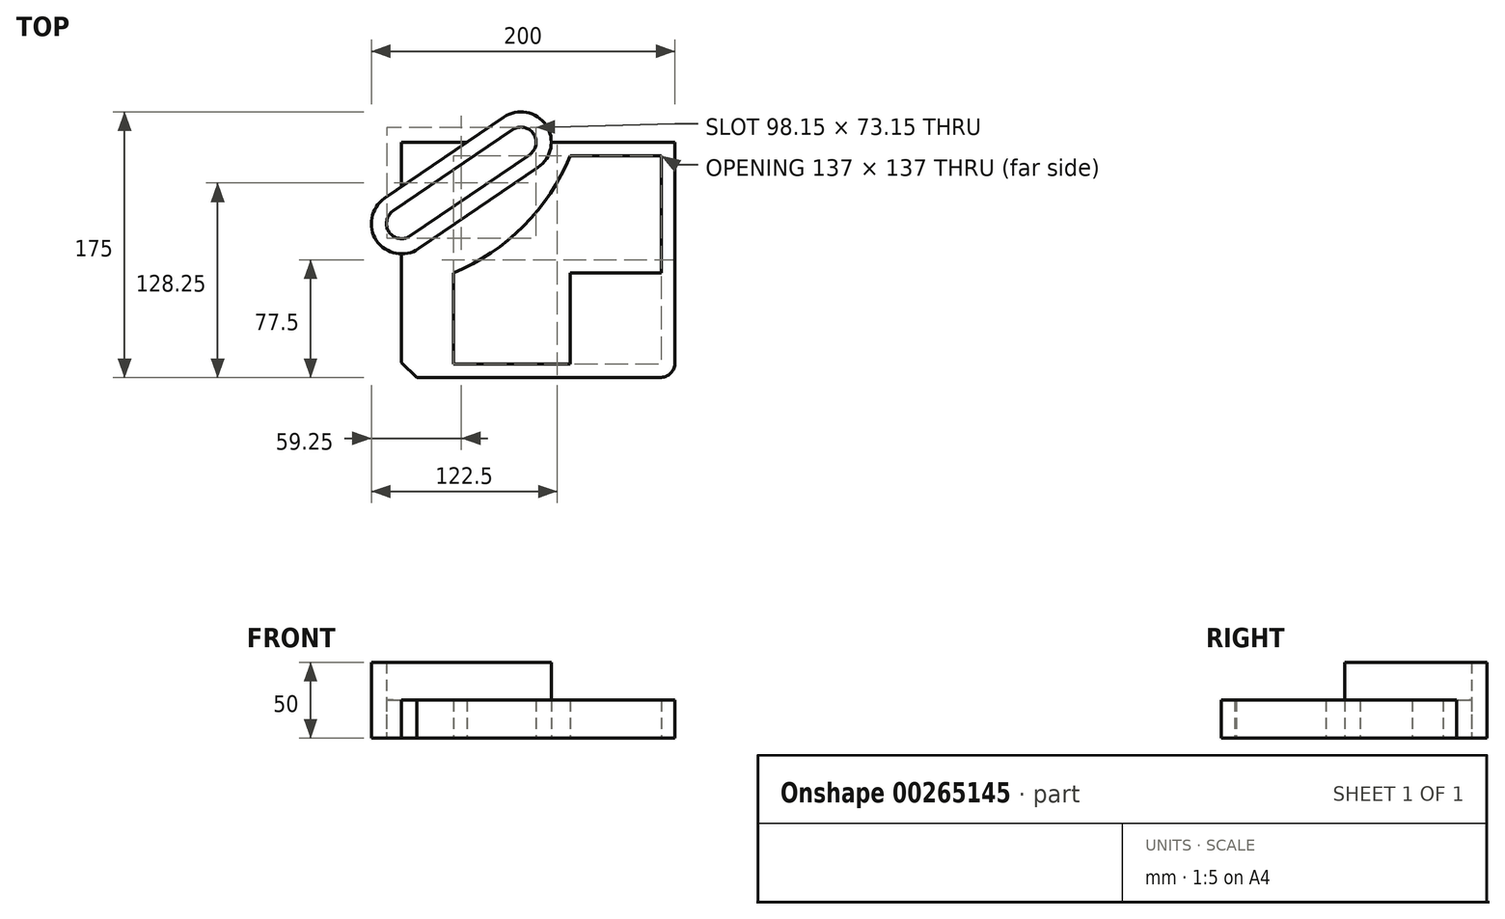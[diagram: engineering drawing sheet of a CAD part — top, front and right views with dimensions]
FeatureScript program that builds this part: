
annotation { "Feature Type Name" : "Feature", "Feature Type Description" : "" }
export const myFeature = defineFeature(function(context is Context, id is Id, definition is map)
    precondition{}
    {
        {
            var Q0;
            Q0=qCreatedBy(makeId("Top.planeOp"),FACE);
            var sketch = newSketch(context, id + "F0", { "sketchPlane" : qUnion([Q0])});
            skLineSegment(sketch, "E0", {"start": v(0, 0) * mm, "end": v(200, 0) * mm});
            skLineSegment(sketch, "E1", {"start": v(210, 10) * mm, "end": v(210, 160) * mm});
            skLineSegment(sketch, "E2", {"start": v(210, 160) * mm, "end": v(170, 200) * mm});
            skLineSegment(sketch, "E3", {"start": v(170, 200) * mm, "end": v(10, 200) * mm});
            skLineSegment(sketch, "E4", {"start": v(0, 190) * mm, "end": v(0, 40) * mm});
            skLineSegment(sketch, "E5", {"start": v(0, 40) * mm, "end": v(40, 0) * mm});
            skPoint(sketch, "E6.visualSharp", {"position": v(0, 200) * mm});
            skArc(sketch, "E6.filletArc", {"start": v(10, 200) * mm, "mid": v(2.93, 197.07) * mm, "end": v(0, 190) * mm});
            skPoint(sketch, "E7.visualSharp", {"position": v(210, 0) * mm});
            skArc(sketch, "E7.filletArc", {"start": v(200, 0) * mm, "mid": v(207.07, 2.93) * mm, "end": v(210, 10) * mm});
            skLineSegment(sketch, "E8", {"start": v(0, 0) * mm, "end": v(161.8, 0) * mm});
            skLineSegment(sketch, "E9", {"start": v(210, 0) * mm, "end": v(30, 0) * mm});
            skLineSegment(sketch, "E10", {"start": v(210, 0) * mm, "end": v(210, 109.1) * mm});
            skLineSegment(sketch, "E11", {"start": v(141, 0) * mm, "end": v(141, 9) * mm});
            skLineSegment(sketch, "E12", {"start": v(141, 9) * mm, "end": v(64, 9) * mm});
            skLineSegment(sketch, "E13", {"start": v(141, 9) * mm, "end": v(141, 69) * mm});
            skLineSegment(sketch, "E14", {"start": v(210, 89.6) * mm, "end": v(201, 89.6) * mm});
            skLineSegment(sketch, "E15", {"start": v(141, 69) * mm, "end": v(201, 69) * mm});
            skLineSegment(sketch, "E16", {"start": v(201, 69) * mm, "end": v(201, 146) * mm});
            skLineSegment(sketch, "E17", {"start": v(201, 146) * mm, "end": v(141, 146) * mm});
            skLineSegment(sketch, "E18", {"start": v(64, 9) * mm, "end": v(64, 69) * mm});
            skArc(sketch, "E19", {"start": v(64, 69) * mm, "mid": v(110.25, 99.75) * mm, "end": v(141, 146) * mm});
            skLineSegment(sketch, "E20", {"start": v(210, 0) * mm, "end": v(210, 155) * mm});
            skLineSegment(sketch, "E21", {"start": v(210, 0) * mm, "end": v(57.89, 0) * mm});
            skLineSegment(sketch, "E22", {"start": v(30, 0) * mm, "end": v(210, 0) * mm});
            skLineSegment(sketch, "E23", {"start": v(30, 0) * mm, "end": v(30, 155) * mm});
            skLineSegment(sketch, "E24", {"start": v(210, 155) * mm, "end": v(30, 155) * mm});
            skPoint(sketch, "E25", {"position": v(108.5, 200) * mm});
            skPoint(sketch, "E26", {"position": v(108.5, 155) * mm});
            skPoint(sketch, "E27", {"position": v(30, 101.5) * mm});
            skArc(sketch, "E28", {"start": v(114.13, 146.74) * mm, "mid": v(116.76, 160.63) * mm, "end": v(102.87, 163.26) * mm});
            skArc(sketch, "E29", {"start": v(35.63, 93.24) * mm, "mid": v(21.74, 95.87) * mm, "end": v(24.37, 109.76) * mm});
            skLineSegment(sketch, "E30", {"start": v(24.37, 109.76) * mm, "end": v(102.87, 163.26) * mm});
            skLineSegment(sketch, "E31", {"start": v(35.63, 93.24) * mm, "end": v(114.13, 146.74) * mm});
            skArc(sketch, "E32", {"start": v(119.76, 138.47) * mm, "mid": v(125.03, 166.26) * mm, "end": v(97.24, 171.53) * mm});
            skArc(sketch, "E33", {"start": v(41.26, 84.97) * mm, "mid": v(13.47, 90.24) * mm, "end": v(18.74, 118.03) * mm});
            skLineSegment(sketch, "E34", {"start": v(18.74, 118.03) * mm, "end": v(97.24, 171.53) * mm});
            skLineSegment(sketch, "E35", {"start": v(41.26, 84.97) * mm, "end": v(119.76, 138.47) * mm});
            skSolve(sketch);
        }
        {
            var Q0;
            {var subQ6=sQuery(id+"F0.wireOp",EDGE,"E1");Q0=makeQuery(id+"F0.imprint","IMPRINT",FACE,{"disambiguationData":[TD([[makeQuery(id+"F0.imprint","IMPRINT",EDGE,{"derivedFrom":subQ6}),1.0]])]});}
            var Q1;
            {var subQ5=sQuery(id+"F0.wireOp",EDGE,"E11");Q1=makeQuery(id+"F0.imprint","IMPRINT",FACE,{"disambiguationData":[TD([[makeQuery(id+"F0.imprint","IMPRINT",EDGE,{"derivedFrom":subQ5}),1.0]])]});}
            var Q2;
            {var subQ2=sQuery(id+"F0.wireOp",EDGE,"E7.filletArc");Q2=makeQuery(id+"F0.imprint","IMPRINT",FACE,{"disambiguationData":[TD([[makeQuery(id+"F0.imprint","IMPRINT",EDGE,{"derivedFrom":subQ2}),1.0]])]});}
            var Q3;
            {var subQ0=sQuery(id+"F0.wireOp",EDGE,"E24");var subQ1=sQuery(id+"F0.wireOp",EDGE,"E23");var subQ2=makeQuery(id+"F0.imprint","INTERSECT",VERTEX,{"derivedFrom":[subQ1,subQ0]});Q3=makeQuery(id+"F0.imprint","IMPRINT",FACE,{"disambiguationData":[TD([[makeQuery(id+"F0.imprint","IMPRINT",EDGE,{"disambiguationData":[TD([[subQ2,1.0]])],"derivedFrom":subQ1}),-1.0]])]});}
            extrude(context, id + "F1", {"entities" : qUnion([Q0, Q1, Q2, Q3]), "depth" : 25 * mm});
        }
        {
            var Q0;
            {var subQ0=sQuery(id+"F0.wireOp",EDGE,"E31");Q0=makeQuery(id+"F0.imprint","IMPRINT",FACE,{"disambiguationData":[TD([[makeQuery(id+"F0.imprint","IMPRINT",EDGE,{"derivedFrom":subQ0}),1.0]])]});}
            var Q1;
            {var subQ0=sQuery(id+"F0.wireOp",EDGE,"E29");var subQ1=sQuery(id+"F0.wireOp",EDGE,"E23");var subQ2=makeQuery(id+"F0.imprint","INTERSECT",VERTEX,{"derivedFrom":[subQ1,subQ0]});Q1=makeQuery(id+"F0.imprint","IMPRINT",FACE,{"disambiguationData":[TD([[makeQuery(id+"F0.imprint","IMPRINT",EDGE,{"disambiguationData":[TD([[subQ2,-1.0]])],"derivedFrom":subQ1}),1.0]])]});}
            var Q2;
            {var subQ0=sQuery(id+"F0.wireOp",EDGE,"E28");var subQ1=sQuery(id+"F0.wireOp",EDGE,"E24");var subQ2=makeQuery(id+"F0.imprint","INTERSECT",VERTEX,{"derivedFrom":[subQ1,subQ0]});Q2=makeQuery(id+"F0.imprint","IMPRINT",FACE,{"disambiguationData":[TD([[makeQuery(id+"F0.imprint","IMPRINT",EDGE,{"disambiguationData":[TD([[subQ2,-1.0]])],"derivedFrom":subQ1}),-1.0]])]});}
            extrude(context, id + "F2", {"entities" : qUnion([Q0, Q1, Q2]), "depth" : 25 * mm});
        }
        {
            var Q0;
            {var subQ3=sQuery(id+"F0.wireOp",EDGE,"E23");var subQ7=sQuery(id+"F0.wireOp",EDGE,"E33");var subQ9=makeQuery(id+"F0.imprint","INTERSECT",VERTEX,{"derivedFrom":[subQ3,subQ7]});Q0=makeQuery(id+"F0.imprint","IMPRINT",FACE,{"disambiguationData":[TD([[makeQuery(id+"F0.imprint","IMPRINT",EDGE,{"disambiguationData":[TD([[subQ9,-1.0]])],"derivedFrom":subQ3}),1.0]])]});}
            var Q1;
            {var subQ0=sQuery(id+"F0.wireOp",EDGE,"E31");Q1=makeQuery(id+"F0.imprint","IMPRINT",FACE,{"disambiguationData":[TD([[makeQuery(id+"F0.imprint","IMPRINT",EDGE,{"derivedFrom":subQ0}),-1.0]])]});}
            var Q2;
            {var subQ3=sQuery(id+"F0.wireOp",EDGE,"E24");var subQ8=sQuery(id+"F0.wireOp",EDGE,"E32");var subQ9=makeQuery(id+"F0.imprint","INTERSECT",VERTEX,{"derivedFrom":[subQ3,subQ8]});Q2=makeQuery(id+"F0.imprint","IMPRINT",FACE,{"disambiguationData":[TD([[makeQuery(id+"F0.imprint","IMPRINT",EDGE,{"disambiguationData":[TD([[subQ9,-1.0]])],"derivedFrom":subQ3}),-1.0]])]});}
            var Q3;
            {var subQ0=sQuery(id+"F0.wireOp",EDGE,"E30");var subQ1=sQuery(id+"F0.wireOp",EDGE,"E23");var subQ2=makeQuery(id+"F0.imprint","INTERSECT",VERTEX,{"derivedFrom":[subQ1,subQ0]});Q3=makeQuery(id+"F0.imprint","IMPRINT",FACE,{"disambiguationData":[TD([[makeQuery(id+"F0.imprint","IMPRINT",EDGE,{"disambiguationData":[TD([[subQ2,-1.0]])],"derivedFrom":subQ1}),-1.0]])]});}
            extrude(context, id + "F3", {"entities" : qUnion([Q0, Q1, Q2, Q3]), "depth" : 50 * mm});
        }
    });
